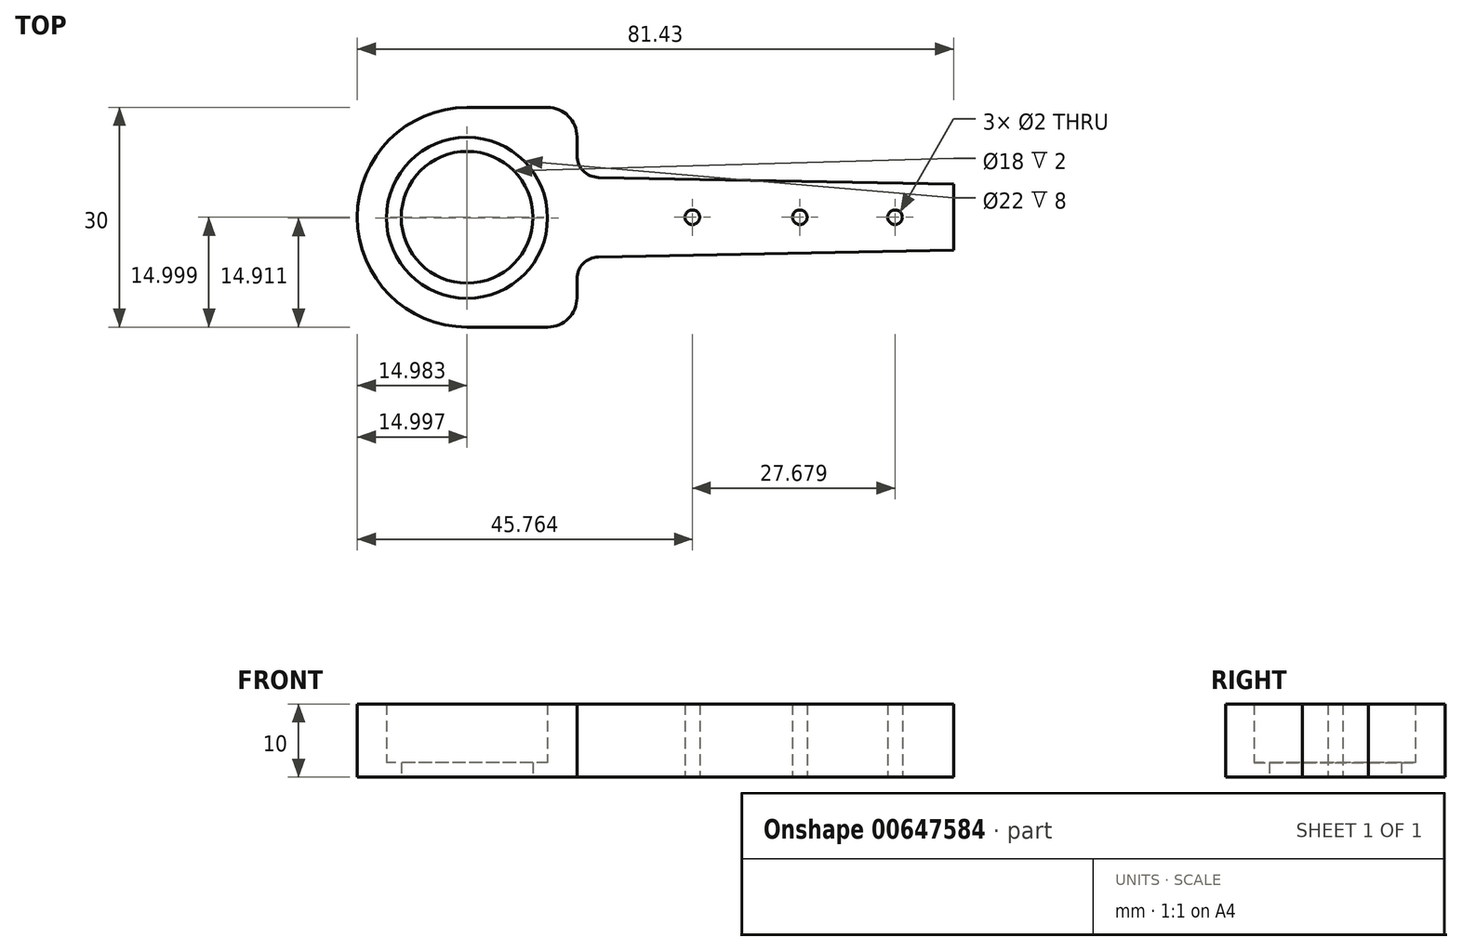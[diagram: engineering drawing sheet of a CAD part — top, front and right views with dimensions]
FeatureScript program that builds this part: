
annotation { "Feature Type Name" : "Feature", "Feature Type Description" : "" }
export const myFeature = defineFeature(function(context is Context, id is Id, definition is map)
    precondition{}
    {
        {
            var Q0;
            Q0=qCreatedBy(makeId("Top.planeOp"),FACE);
            var sketch = newSketch(context, id + "F0", { "sketchPlane" : qUnion([Q0])});
            skLineSegment(sketch, "E0", {"start": v(-18.61, 6.36) * mm, "end": v(-18.61, 6.36) * mm});
            skLineSegment(sketch, "E1", {"start": v(-3.61, 21.36) * mm, "end": v(7.39, 21.36) * mm});
            skLineSegment(sketch, "E2", {"start": v(11.39, 17.36) * mm, "end": v(11.39, 14.8) * mm});
            skLineSegment(sketch, "E3", {"start": v(14.33, 11.8) * mm, "end": v(62.82, 10.86) * mm});
            skLineSegment(sketch, "E4", {"start": v(62.82, 10.86) * mm, "end": v(62.82, 1.86) * mm});
            skLineSegment(sketch, "E5", {"start": v(62.82, 1.86) * mm, "end": v(14.33, 0.92) * mm});
            skLineSegment(sketch, "E6", {"start": v(11.39, -2.08) * mm, "end": v(11.39, -4.64) * mm});
            skLineSegment(sketch, "E7", {"start": v(7.39, -8.64) * mm, "end": v(-3.61, -8.64) * mm});
            skPoint(sketch, "E8.visualSharp", {"position": v(11.39, 11.86) * mm});
            skArc(sketch, "E8.filletArc", {"start": v(11.39, 14.8) * mm, "mid": v(12.25, 12.7) * mm, "end": v(14.33, 11.8) * mm});
            skPoint(sketch, "E9.visualSharp", {"position": v(11.39, 0.86) * mm});
            skArc(sketch, "E9.filletArc", {"start": v(14.33, 0.92) * mm, "mid": v(12.25, 0.02) * mm, "end": v(11.39, -2.08) * mm});
            skLineSegment(sketch, "E10", {"start": v(-18.61, 6.36) * mm, "end": v(62.82, 6.36) * mm, "construction": true});
            skCircle(sketch, "E11", {"center": v(-3.61, 6.36) * mm, "radius": 9 * mm});
            skCircle(sketch, "E12", {"center": v(27.15, 6.36) * mm, "radius": 1 * mm});
            skCircle(sketch, "E13", {"center": v(41.83, 6.36) * mm, "radius": 1 * mm});
            skCircle(sketch, "E14", {"center": v(54.83, 6.36) * mm, "radius": 1 * mm});
            skPoint(sketch, "E15.visualSharp", {"position": v(-18.61, 21.36) * mm});
            skArc(sketch, "E15.filletArc", {"start": v(-3.61, 21.36) * mm, "mid": v(-14.22, 16.97) * mm, "end": v(-18.61, 6.36) * mm});
            skPoint(sketch, "E16.visualSharp", {"position": v(-18.61, -8.64) * mm});
            skArc(sketch, "E16.filletArc", {"start": v(-18.61, 6.36) * mm, "mid": v(-14.22, -4.25) * mm, "end": v(-3.61, -8.64) * mm});
            skPoint(sketch, "E17.visualSharp", {"position": v(11.39, 21.36) * mm});
            skArc(sketch, "E17.filletArc", {"start": v(11.39, 17.36) * mm, "mid": v(10.22, 20.19) * mm, "end": v(7.39, 21.36) * mm});
            skPoint(sketch, "E18.visualSharp", {"position": v(11.39, -8.64) * mm});
            skArc(sketch, "E18.filletArc", {"start": v(7.39, -8.64) * mm, "mid": v(10.22, -7.47) * mm, "end": v(11.39, -4.64) * mm});
            skSolve(sketch);
        }
        {
            var Q0;
            Q0 = qSketchRegion(id + "F0", true);
            extrude(context, id + "F1", {"entities" : qUnion([Q0]), "depth" : 2 * mm, "offsetDistance" : 25 * mm});
        }
        {
            var Q0;
            Q0=qCreatedBy(makeId("Top.planeOp"),FACE);
            cPlane(context, id + "F2", {"entities" : qUnion([Q0]), "cplaneType" : CPlaneType.OFFSET, "offset" : 2 * mm, "width" : 150 * mm, "height" : 150 * mm});
        }
        {
            var Q0;
            Q0=qCreatedBy(id+"F2.planeOp",FACE);
            var sketch = newSketch(context, id + "F3", { "sketchPlane" : qUnion([Q0])});
            skPoint(sketch, "E19", {"position": v(-3.63, 6.27) * mm});
            skCircle(sketch, "E20", {"center": v(-3.63, 6.27) * mm, "radius": 11 * mm});
            skSolve(sketch);
        }
        {
            var Q0;
            Q0=makeQuery(id+"F1.opExtrude","CAP_FACE",FACE,{"disambiguationData":[OSD([sQuery(id+"F0.wireOp",EDGE,"E1"),sQuery(id+"F0.wireOp",EDGE,"E2"),sQuery(id+"F0.wireOp",EDGE,"E3"),sQuery(id+"F0.wireOp",EDGE,"E4"),sQuery(id+"F0.wireOp",EDGE,"E5"),sQuery(id+"F0.wireOp",EDGE,"E6"),sQuery(id+"F0.wireOp",EDGE,"E7"),sQuery(id+"F0.wireOp",EDGE,"E8.filletArc"),sQuery(id+"F0.wireOp",EDGE,"E9.filletArc"),sQuery(id+"F0.wireOp",EDGE,"E11"),sQuery(id+"F0.wireOp",EDGE,"E12"),sQuery(id+"F0.wireOp",EDGE,"E13"),sQuery(id+"F0.wireOp",EDGE,"E14"),sQuery(id+"F0.wireOp",EDGE,"E15.filletArc"),sQuery(id+"F0.wireOp",EDGE,"E16.filletArc"),sQuery(id+"F0.wireOp",EDGE,"E17.filletArc"),sQuery(id+"F0.wireOp",EDGE,"E18.filletArc")])],"isStart":false});
            extrude(context, id + "F4", {"entities" : qUnion([Q0]), "operationType" : NewBodyOperationType.ADD, "depth" : 8 * mm, "offsetDistance" : 25 * mm});
        }
        {
            var Q0;
            Q0=makeQuery(id+"F3.imprint","IMPRINT",FACE,{"disambiguationData":[TD([[makeQuery(id+"F3.imprint","IMPRINT",EDGE,{"derivedFrom":sQuery(id+"F3.wireOp",EDGE,"E20")}),1.0]])]});
            extrude(context, id + "F5", {"entities" : qUnion([Q0]), "operationType" : NewBodyOperationType.REMOVE, "depth" : 8 * mm, "offsetDistance" : 25 * mm});
        }
    });
